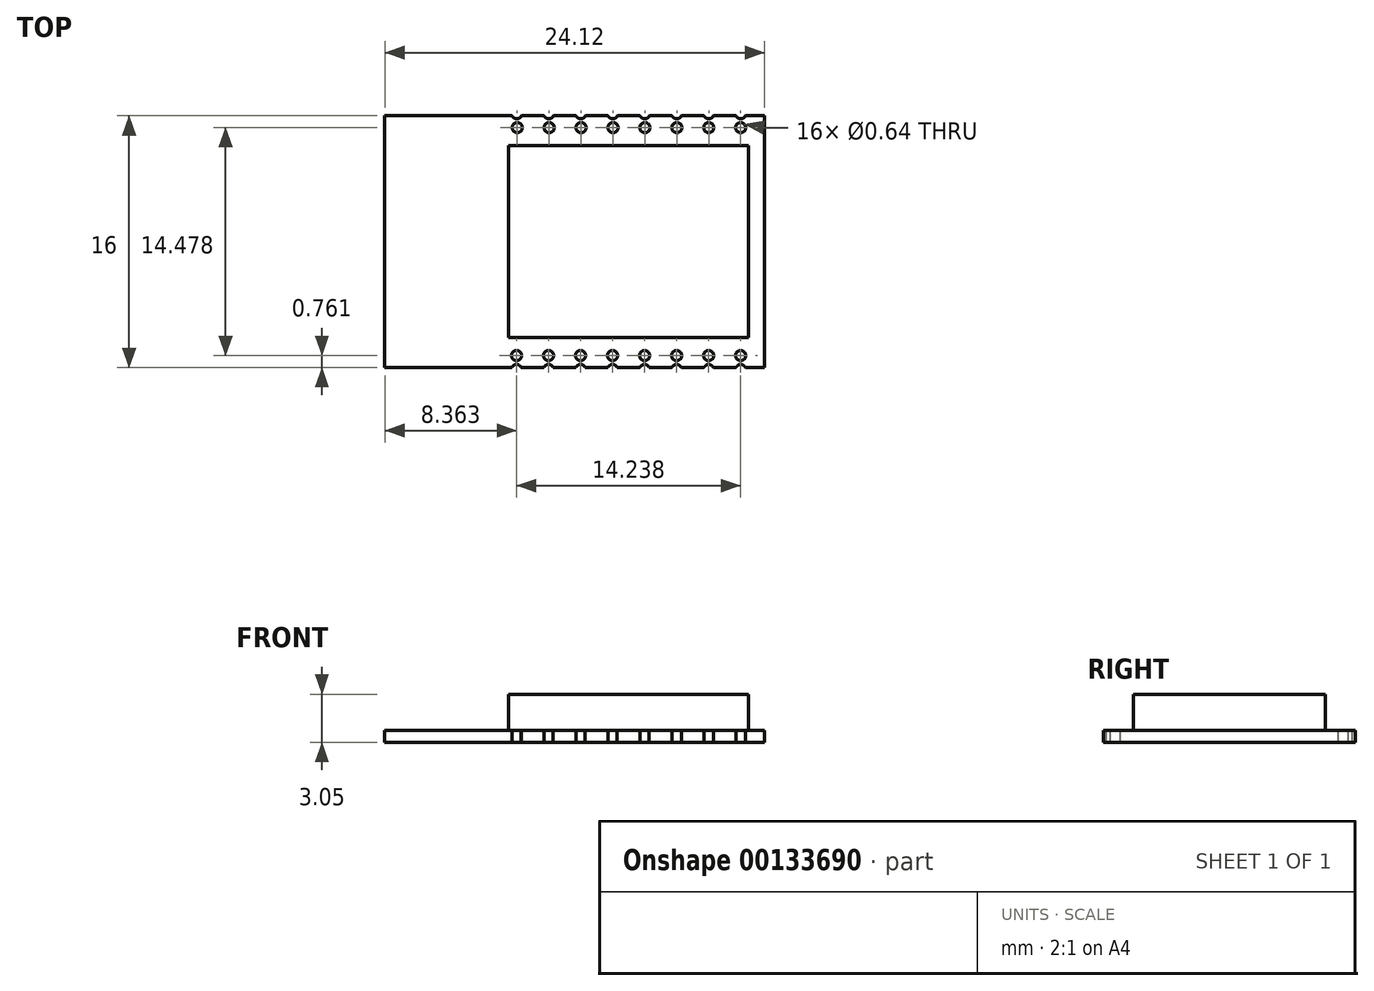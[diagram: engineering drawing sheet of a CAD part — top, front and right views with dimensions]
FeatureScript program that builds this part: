
annotation { "Feature Type Name" : "Feature", "Feature Type Description" : "" }
export const myFeature = defineFeature(function(context is Context, id is Id, definition is map)
    precondition{}
    {
        {
            var Q0;
            Q0=qCreatedBy(makeId("Top.planeOp"),FACE);
            var sketch = newSketch(context, id + "F0", { "sketchPlane" : qUnion([Q0])});
            skLineSegment(sketch, "E0.bottom", {"start": v(12.07, 8) * mm, "end": v(-12.07, 8) * mm});
            skLineSegment(sketch, "E0.top", {"start": v(12.06, -8) * mm, "end": v(-12.07, -8) * mm});
            skLineSegment(sketch, "E0.left", {"start": v(12.07, 8) * mm, "end": v(12.06, -8) * mm});
            skLineSegment(sketch, "E0.right", {"start": v(-12.07, 8) * mm, "end": v(-12.07, -8) * mm});
            skLineSegment(sketch, "E1.bottom", {"start": v(-4.2, 6.1) * mm, "end": v(11.05, 6.1) * mm});
            skLineSegment(sketch, "E1.top", {"start": v(-4.2, -6.1) * mm, "end": v(11.05, -6.1) * mm});
            skLineSegment(sketch, "E1.left", {"start": v(-4.2, 6.1) * mm, "end": v(-4.2, -6.1) * mm});
            skLineSegment(sketch, "E1.right", {"start": v(11.05, 6.1) * mm, "end": v(11.05, -6.1) * mm});
            skCircle(sketch, "E2", {"center": v(10.54, 8.13) * mm, "radius": 0.32 * mm});
            skCircle(sketch, "E3", {"center": v(10.54, 7.24) * mm, "radius": 0.32 * mm});
            skLineSegment(sketch, "E4", {"start": v(17.85, 8.13) * mm, "end": v(-15.06, 8.13) * mm, "construction": true});
            skLineSegment(sketch, "E5", {"start": v(17.85, 7.24) * mm, "end": v(-15.06, 7.24) * mm, "construction": true});
            skCircle(sketch, "E6.1.0.0", {"center": v(8.5, 8.13) * mm, "radius": 0.32 * mm});
            skCircle(sketch, "E6.2.0.0", {"center": v(6.48, 8.13) * mm, "radius": 0.32 * mm});
            skCircle(sketch, "E6.3.0.0", {"center": v(4.44, 8.13) * mm, "radius": 0.32 * mm});
            skCircle(sketch, "E6.4.0.0", {"center": v(2.41, 8.13) * mm, "radius": 0.32 * mm});
            skCircle(sketch, "E6.5.0.0", {"center": v(0.38, 8.13) * mm, "radius": 0.32 * mm});
            skCircle(sketch, "E6.6.0.0", {"center": v(-1.65, 8.13) * mm, "radius": 0.32 * mm});
            skCircle(sketch, "E6.7.0.0", {"center": v(-3.68, 8.13) * mm, "radius": 0.32 * mm});
            skLineSegment(sketch, "E6.direction1", {"start": v(10.54, 8.13) * mm, "end": v(8.5, 8.13) * mm, "construction": true});
            skCircle(sketch, "E7.1.0.0", {"center": v(8.51, 7.24) * mm, "radius": 0.32 * mm});
            skCircle(sketch, "E7.2.0.0", {"center": v(6.49, 7.24) * mm, "radius": 0.32 * mm});
            skCircle(sketch, "E7.3.0.0", {"center": v(4.46, 7.24) * mm, "radius": 0.32 * mm});
            skCircle(sketch, "E7.4.0.0", {"center": v(2.43, 7.24) * mm, "radius": 0.32 * mm});
            skCircle(sketch, "E7.5.0.0", {"center": v(0.4, 7.24) * mm, "radius": 0.32 * mm});
            skCircle(sketch, "E7.6.0.0", {"center": v(-1.62, 7.24) * mm, "radius": 0.32 * mm});
            skCircle(sketch, "E7.7.0.0", {"center": v(-3.65, 7.24) * mm, "radius": 0.32 * mm});
            skLineSegment(sketch, "E7.direction1", {"start": v(10.54, 7.24) * mm, "end": v(8.51, 7.24) * mm, "construction": true});
            skLineSegment(sketch, "E8", {"start": v(18, -7.24) * mm, "end": v(-15.09, -7.24) * mm, "construction": true});
            skLineSegment(sketch, "E9", {"start": v(18, -8.13) * mm, "end": v(-15.09, -8.13) * mm, "construction": true});
            skCircle(sketch, "E10", {"center": v(10.54, -7.24) * mm, "radius": 0.32 * mm});
            skCircle(sketch, "E11", {"center": v(10.54, -8.13) * mm, "radius": 0.32 * mm});
            skCircle(sketch, "E12.1.0.0", {"center": v(8.5, -7.24) * mm, "radius": 0.32 * mm});
            skCircle(sketch, "E12.2.0.0", {"center": v(6.47, -7.24) * mm, "radius": 0.32 * mm});
            skCircle(sketch, "E12.3.0.0", {"center": v(4.44, -7.24) * mm, "radius": 0.32 * mm});
            skCircle(sketch, "E12.4.0.0", {"center": v(2.4, -7.24) * mm, "radius": 0.32 * mm});
            skCircle(sketch, "E12.5.0.0", {"center": v(0.37, -7.24) * mm, "radius": 0.32 * mm});
            skCircle(sketch, "E12.6.0.0", {"center": v(-1.66, -7.24) * mm, "radius": 0.32 * mm});
            skCircle(sketch, "E12.7.0.0", {"center": v(-3.7, -7.24) * mm, "radius": 0.32 * mm});
            skLineSegment(sketch, "E12.direction1", {"start": v(10.54, -7.24) * mm, "end": v(8.5, -7.24) * mm, "construction": true});
            skCircle(sketch, "E13.1.0.0", {"center": v(8.5, -8.13) * mm, "radius": 0.32 * mm});
            skCircle(sketch, "E13.2.0.0", {"center": v(6.47, -8.13) * mm, "radius": 0.32 * mm});
            skCircle(sketch, "E13.3.0.0", {"center": v(4.44, -8.13) * mm, "radius": 0.32 * mm});
            skCircle(sketch, "E13.4.0.0", {"center": v(2.4, -8.13) * mm, "radius": 0.32 * mm});
            skCircle(sketch, "E13.5.0.0", {"center": v(0.37, -8.13) * mm, "radius": 0.32 * mm});
            skCircle(sketch, "E13.6.0.0", {"center": v(-1.66, -8.13) * mm, "radius": 0.32 * mm});
            skCircle(sketch, "E13.7.0.0", {"center": v(-3.7, -8.13) * mm, "radius": 0.32 * mm});
            skLineSegment(sketch, "E13.direction1", {"start": v(10.54, -8.13) * mm, "end": v(8.5, -8.13) * mm, "construction": true});
            skSolve(sketch);
        }
        {
            var Q0;
            Q0=makeQuery(id+"F0.imprint","IMPRINT",FACE,{"disambiguationData":[TD([[makeQuery(id+"F0.imprint","IMPRINT",EDGE,{"derivedFrom":sQuery(id+"F0.wireOp",EDGE,"E0.bottom")}),1.0]])]});
            var Q1;
            Q1=makeQuery(id+"F0.imprint","IMPRINT",FACE,{"disambiguationData":[TD([[makeQuery(id+"F0.imprint","IMPRINT",EDGE,{"derivedFrom":sQuery(id+"F0.wireOp",EDGE,"E1.bottom")}),-1.0]])]});
            extrude(context, id + "F1", {"entities" : qUnion([Q0, Q1]), "oppositeDirection" : true, "depth" : 0.76 * mm});
        }
        {
            var Q0;
            Q0=makeQuery(id+"F0.imprint","IMPRINT",FACE,{"disambiguationData":[TD([[makeQuery(id+"F0.imprint","IMPRINT",EDGE,{"derivedFrom":sQuery(id+"F0.wireOp",EDGE,"E1.bottom")}),-1.0]])]});
            extrude(context, id + "F2", {"entities" : qUnion([Q0]), "operationType" : NewBodyOperationType.ADD, "depth" : 2.3 * mm});
        }
    });
